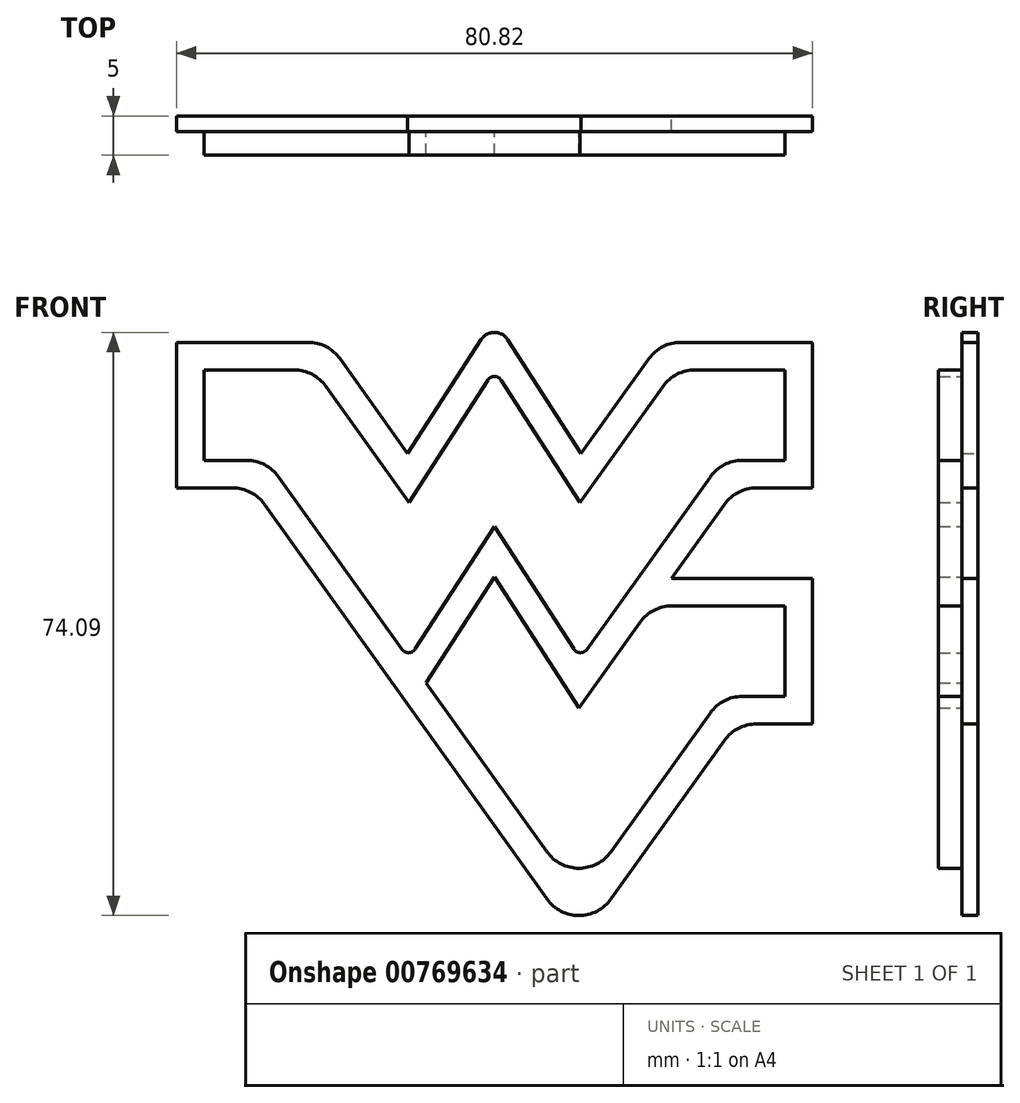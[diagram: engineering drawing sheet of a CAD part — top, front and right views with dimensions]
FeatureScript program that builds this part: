
annotation { "Feature Type Name" : "Feature", "Feature Type Description" : "" }
export const myFeature = defineFeature(function(context is Context, id is Id, definition is map)
    precondition{}
    {
        {
            var Q0;
            Q0=qCreatedBy(makeId("Front.planeOp"),FACE);
            var sketch = newSketch(context, id + "F0", { "sketchPlane" : qUnion([Q0])});
            skLineSegment(sketch, "E0", {"start": v(0, 0) * mm, "end": v(0, -11.5) * mm});
            skLineSegment(sketch, "E1", {"start": v(0, -11.5) * mm, "end": v(5.43, -11.5) * mm});
            skLineSegment(sketch, "E2", {"start": v(0, 0) * mm, "end": v(11.43, 0) * mm});
            skLineSegment(sketch, "E3", {"start": v(15.5, -2.1) * mm, "end": v(26.04, -16.83) * mm});
            skLineSegment(sketch, "E4", {"start": v(26.04, -16.83) * mm, "end": v(0, 0) * mm});
            skLineSegment(sketch, "E5", {"start": v(9.5, -13.6) * mm, "end": v(25.18, -35.52) * mm});
            skLineSegment(sketch, "E6", {"start": v(26.04, -16.83) * mm, "end": v(26.04, -36.71) * mm});
            skLineSegment(sketch, "E7", {"start": v(26.04, -16.83) * mm, "end": v(36.07, -1.3) * mm});
            skLineSegment(sketch, "E8", {"start": v(36.9, 0) * mm, "end": v(36.9, -19.89) * mm});
            skLineSegment(sketch, "E9", {"start": v(36.9, -19.89) * mm, "end": v(26.83, -35.48) * mm});
            skLineSegment(sketch, "E10.MirrorCS", {"start": v(47.78, -16.83) * mm, "end": v(37.75, -1.3) * mm});
            skLineSegment(sketch, "E11.MirrorCS", {"start": v(36.9, -19.89) * mm, "end": v(46.98, -35.48) * mm});
            skLineSegment(sketch, "E12.MirrorCS", {"start": v(47.78, -16.83) * mm, "end": v(47.78, -36.71) * mm});
            skLineSegment(sketch, "E13.MirrorCS", {"start": v(58.32, -2.1) * mm, "end": v(47.78, -16.83) * mm});
            skLineSegment(sketch, "E14.MirrorCS", {"start": v(73.82, 0) * mm, "end": v(62.4, 0) * mm});
            skLineSegment(sketch, "E15.MirrorCS", {"start": v(73.82, -11.5) * mm, "end": v(68.4, -11.5) * mm});
            skLineSegment(sketch, "E16.MirrorCS", {"start": v(73.82, 0) * mm, "end": v(73.82, -11.5) * mm});
            skLineSegment(sketch, "E17.MirrorCS", {"start": v(64.32, -13.6) * mm, "end": v(48.64, -35.52) * mm});
            skLineSegment(sketch, "E18.0", {"start": v(-3.5, 3.5) * mm, "end": v(-3.5, -15) * mm});
            skLineSegment(sketch, "E18.1", {"start": v(-3.5, -15) * mm, "end": v(3.63, -15) * mm});
            skLineSegment(sketch, "E18.2", {"start": v(7.7, -17.1) * mm, "end": v(26.18, -42.93) * mm});
            skLineSegment(sketch, "E18.3", {"start": v(56.52, 1.4) * mm, "end": v(47.93, -10.6) * mm});
            skLineSegment(sketch, "E18.4", {"start": v(47.93, -10.6) * mm, "end": v(38.59, 3.85) * mm});
            skLineSegment(sketch, "E18.5", {"start": v(25.89, -10.6) * mm, "end": v(35.23, 3.85) * mm});
            skLineSegment(sketch, "E18.6", {"start": v(17.3, 1.4) * mm, "end": v(25.89, -10.6) * mm});
            skLineSegment(sketch, "E18.7", {"start": v(77.32, 3.5) * mm, "end": v(60.6, 3.5) * mm});
            skLineSegment(sketch, "E18.8", {"start": v(77.32, 3.5) * mm, "end": v(77.32, -15) * mm});
            skLineSegment(sketch, "E18.9", {"start": v(77.32, -15) * mm, "end": v(70.19, -15) * mm});
            skLineSegment(sketch, "E18.10", {"start": v(-3.5, 3.5) * mm, "end": v(13.23, 3.5) * mm});
            skLineSegment(sketch, "E18.11", {"start": v(66.12, -17.1) * mm, "end": v(47.64, -42.93) * mm});
            skLineSegment(sketch, "E18.12", {"start": v(36.9, -26.34) * mm, "end": v(47.64, -42.93) * mm});
            skLineSegment(sketch, "E18.13", {"start": v(36.9, -26.34) * mm, "end": v(26.18, -42.93) * mm});
            skPoint(sketch, "E19.visualSharp", {"position": v(14, 0) * mm});
            skArc(sketch, "E19.filletArc", {"start": v(15.5, -2.1) * mm, "mid": v(13.72, -0.55) * mm, "end": v(11.43, 0) * mm});
            skPoint(sketch, "E20.visualSharp", {"position": v(8, -11.5) * mm});
            skArc(sketch, "E20.filletArc", {"start": v(9.5, -13.6) * mm, "mid": v(7.72, -12.05) * mm, "end": v(5.43, -11.5) * mm});
            skPoint(sketch, "E21.visualSharp", {"position": v(26.04, -36.71) * mm});
            skArc(sketch, "E21.filletArc", {"start": v(25.18, -35.52) * mm, "mid": v(26.02, -35.94) * mm, "end": v(26.83, -35.48) * mm});
            skPoint(sketch, "E22.visualSharp", {"position": v(47.78, -36.71) * mm});
            skArc(sketch, "E22.filletArc", {"start": v(46.98, -35.48) * mm, "mid": v(47.8, -35.94) * mm, "end": v(48.64, -35.52) * mm});
            skPoint(sketch, "E23.visualSharp", {"position": v(36.9, 0) * mm});
            skArc(sketch, "E23.filletArc", {"start": v(37.75, -1.3) * mm, "mid": v(36.9, -0.84) * mm, "end": v(36.07, -1.3) * mm});
            skPoint(sketch, "E24.visualSharp", {"position": v(65.82, -11.5) * mm});
            skArc(sketch, "E24.filletArc", {"start": v(68.4, -11.5) * mm, "mid": v(66.1, -12.05) * mm, "end": v(64.32, -13.6) * mm});
            skPoint(sketch, "E25.visualSharp", {"position": v(59.82, 0) * mm});
            skArc(sketch, "E25.filletArc", {"start": v(62.4, 0) * mm, "mid": v(60.1, -0.55) * mm, "end": v(58.32, -2.1) * mm});
            skLineSegment(sketch, "E26", {"start": v(26.18, -42.93) * mm, "end": v(43.57, -67.24) * mm});
            skLineSegment(sketch, "E27", {"start": v(26.04, -36.71) * mm, "end": v(43.57, -61.22) * mm});
            skLineSegment(sketch, "E28", {"start": v(51.7, -61.22) * mm, "end": v(64.32, -43.58) * mm});
            skLineSegment(sketch, "E29", {"start": v(68.4, -41.49) * mm, "end": v(73.82, -41.49) * mm});
            skLineSegment(sketch, "E30", {"start": v(73.82, -41.49) * mm, "end": v(73.82, -29.99) * mm});
            skLineSegment(sketch, "E31", {"start": v(73.82, -29.99) * mm, "end": v(59.47, -29.99) * mm});
            skLineSegment(sketch, "E32.0", {"start": v(77.32, -26.49) * mm, "end": v(59.4, -26.49) * mm});
            skLineSegment(sketch, "E32.1", {"start": v(77.32, -44.99) * mm, "end": v(77.32, -26.49) * mm});
            skLineSegment(sketch, "E32.2", {"start": v(70.19, -44.99) * mm, "end": v(77.32, -44.99) * mm});
            skLineSegment(sketch, "E32.3", {"start": v(51.7, -67.24) * mm, "end": v(66.12, -47.08) * mm});
            skPoint(sketch, "E33.visualSharp", {"position": v(47.64, -72.92) * mm});
            skArc(sketch, "E33.filletArc", {"start": v(43.57, -67.24) * mm, "mid": v(47.64, -69.33) * mm, "end": v(51.7, -67.24) * mm});
            skPoint(sketch, "E34.visualSharp", {"position": v(47.64, -66.9) * mm});
            skArc(sketch, "E34.filletArc", {"start": v(43.57, -61.22) * mm, "mid": v(47.64, -63.31) * mm, "end": v(51.7, -61.22) * mm});
            skPoint(sketch, "E35.visualSharp", {"position": v(65.82, -41.49) * mm});
            skArc(sketch, "E35.filletArc", {"start": v(68.4, -41.49) * mm, "mid": v(66.1, -42.04) * mm, "end": v(64.32, -43.58) * mm});
            skPoint(sketch, "E36.visualSharp", {"position": v(67.62, -44.99) * mm});
            skArc(sketch, "E36.filletArc", {"start": v(70.19, -44.99) * mm, "mid": v(67.9, -45.54) * mm, "end": v(66.12, -47.08) * mm});
            skPoint(sketch, "E37.visualSharp", {"position": v(67.62, -15) * mm});
            skArc(sketch, "E37.filletArc", {"start": v(70.19, -15) * mm, "mid": v(67.9, -15.55) * mm, "end": v(66.12, -17.1) * mm});
            skPoint(sketch, "E38.visualSharp", {"position": v(6.2, -15) * mm});
            skArc(sketch, "E38.filletArc", {"start": v(7.7, -17.1) * mm, "mid": v(5.92, -15.55) * mm, "end": v(3.63, -15) * mm});
            skLineSegment(sketch, "E39", {"start": v(47.64, -42.93) * mm, "end": v(55.4, -32.08) * mm});
            skPoint(sketch, "E40.visualSharp", {"position": v(56.9, -29.99) * mm});
            skArc(sketch, "E40.filletArc", {"start": v(59.47, -29.99) * mm, "mid": v(57.18, -30.54) * mm, "end": v(55.4, -32.08) * mm});
            skPoint(sketch, "E41.visualSharp", {"position": v(58.02, 3.5) * mm});
            skArc(sketch, "E41.filletArc", {"start": v(60.6, 3.5) * mm, "mid": v(58.3, 2.95) * mm, "end": v(56.52, 1.4) * mm});
            skPoint(sketch, "E42.visualSharp", {"position": v(15.8, 3.5) * mm});
            skArc(sketch, "E42.filletArc", {"start": v(17.3, 1.4) * mm, "mid": v(15.52, 2.95) * mm, "end": v(13.23, 3.5) * mm});
            skPoint(sketch, "E43.visualSharp", {"position": v(36.9, 6.45) * mm});
            skArc(sketch, "E43.filletArc", {"start": v(38.59, 3.85) * mm, "mid": v(36.9, 4.76) * mm, "end": v(35.23, 3.85) * mm});
            skSolve(sketch);
        }
        {
            var Q0;
            Q0=makeQuery(id+"F0.imprint","IMPRINT",FACE,{"disambiguationData":[TD([[makeQuery(id+"F0.imprint","IMPRINT",EDGE,{"derivedFrom":sQuery(id+"F0.wireOp",EDGE,"E0")}),1.0]])]});
            var Q1;
            Q1=makeQuery(id+"F0.imprint","IMPRINT",FACE,{"disambiguationData":[TD([[makeQuery(id+"F0.imprint","IMPRINT",EDGE,{"derivedFrom":sQuery(id+"F0.wireOp",EDGE,"E2")}),-1.0]])]});
            var Q2;
            {var subQ2=sQuery(id+"F0.wireOp",EDGE,"E7");Q2=makeQuery(id+"F0.imprint","IMPRINT",FACE,{"disambiguationData":[TD([[makeQuery(id+"F0.imprint","IMPRINT",EDGE,{"derivedFrom":subQ2}),-1.0]])]});}
            var Q3;
            {var subQ1=sQuery(id+"F0.wireOp",EDGE,"E10.MirrorCS");Q3=makeQuery(id+"F0.imprint","IMPRINT",FACE,{"disambiguationData":[TD([[makeQuery(id+"F0.imprint","IMPRINT",EDGE,{"derivedFrom":subQ1}),1.0]])]});}
            var Q4;
            {var subQ0=sQuery(id+"F0.wireOp",EDGE,"E13.MirrorCS");Q4=makeQuery(id+"F0.imprint","IMPRINT",FACE,{"disambiguationData":[TD([[makeQuery(id+"F0.imprint","IMPRINT",EDGE,{"derivedFrom":subQ0}),1.0]])]});}
            var Q5;
            {var subQ2=sQuery(id+"F0.wireOp",EDGE,"E18.12");Q5=makeQuery(id+"F0.imprint","IMPRINT",FACE,{"disambiguationData":[TD([[makeQuery(id+"F0.imprint","IMPRINT",EDGE,{"derivedFrom":subQ2}),-1.0]])]});}
            extrude(context, id + "F1", {"entities" : qUnion([Q0, Q1, Q2, Q3, Q4, Q5]), "depth" : 5 * mm, "offsetDistance" : 25 * mm});
        }
        {
            var Q0;
            Q0=makeQuery(id+"F0.imprint","IMPRINT",FACE,{"disambiguationData":[TD([[makeQuery(id+"F0.imprint","IMPRINT",EDGE,{"derivedFrom":sQuery(id+"F0.wireOp",EDGE,"E0")}),-1.0]])]});
            var Q1;
            {var subQ7=sQuery(id+"F0.wireOp",EDGE,"E26");Q1=makeQuery(id+"F0.imprint","IMPRINT",FACE,{"disambiguationData":[TD([[makeQuery(id+"F0.imprint","IMPRINT",EDGE,{"derivedFrom":subQ7}),1.0]])]});}
            extrude(context, id + "F2", {"entities" : qUnion([Q0, Q1]), "operationType" : NewBodyOperationType.ADD, "depth" : 2 * mm, "offsetDistance" : 25 * mm});
        }
    });
